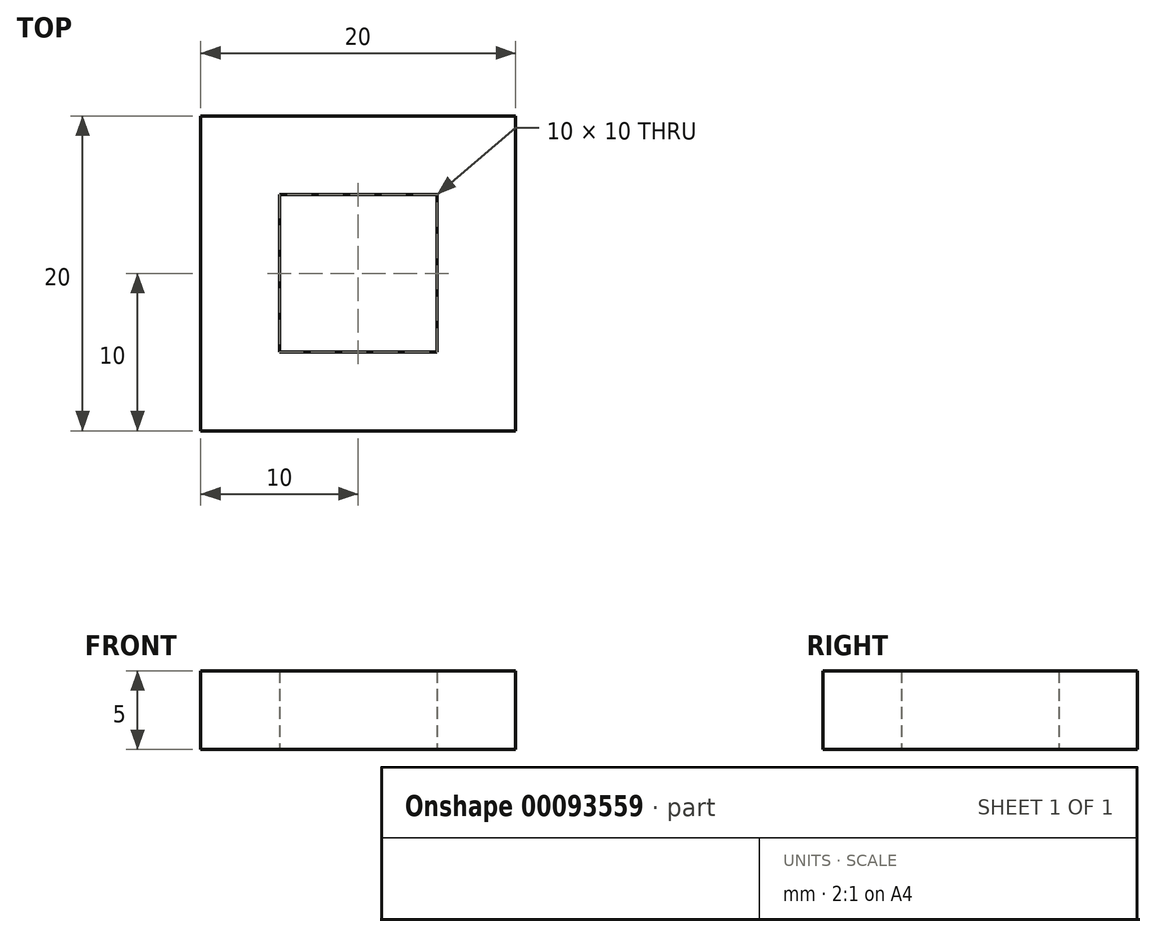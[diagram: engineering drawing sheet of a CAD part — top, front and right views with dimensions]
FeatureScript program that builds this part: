
annotation { "Feature Type Name" : "Feature", "Feature Type Description" : "" }
export const myFeature = defineFeature(function(context is Context, id is Id, definition is map)
    precondition{}
    {
        {
            var Q0;
            Q0=qCreatedBy(makeId("Top.planeOp"),FACE);
            var sketch = newSketch(context, id + "F0", { "sketchPlane" : qUnion([Q0])});
            skLineSegment(sketch, "E0.bottom", {"start": v(5, -5) * mm, "end": v(-5, -5) * mm});
            skLineSegment(sketch, "E0.top", {"start": v(5, 5) * mm, "end": v(-5, 5) * mm});
            skLineSegment(sketch, "E0.left", {"start": v(5, -5) * mm, "end": v(5, 5) * mm});
            skLineSegment(sketch, "E0.right", {"start": v(-5, -5) * mm, "end": v(-5, 5) * mm});
            skPoint(sketch, "E0.middle", {"position": v(0, 0) * mm});
            skLineSegment(sketch, "E1.bottom", {"start": v(10, -10) * mm, "end": v(-10, -10) * mm});
            skLineSegment(sketch, "E1.top", {"start": v(10, 10) * mm, "end": v(-10, 10) * mm});
            skLineSegment(sketch, "E1.left", {"start": v(10, -10) * mm, "end": v(10, 10) * mm});
            skLineSegment(sketch, "E1.right", {"start": v(-10, -10) * mm, "end": v(-10, 10) * mm});
            skSolve(sketch);
        }
        {
            var Q0;
            Q0 = qSketchRegion(id + "F0", true);
            extrude(context, id + "F1", {"entities" : qUnion([Q0]), "depth" : 5 * mm});
        }
    });
